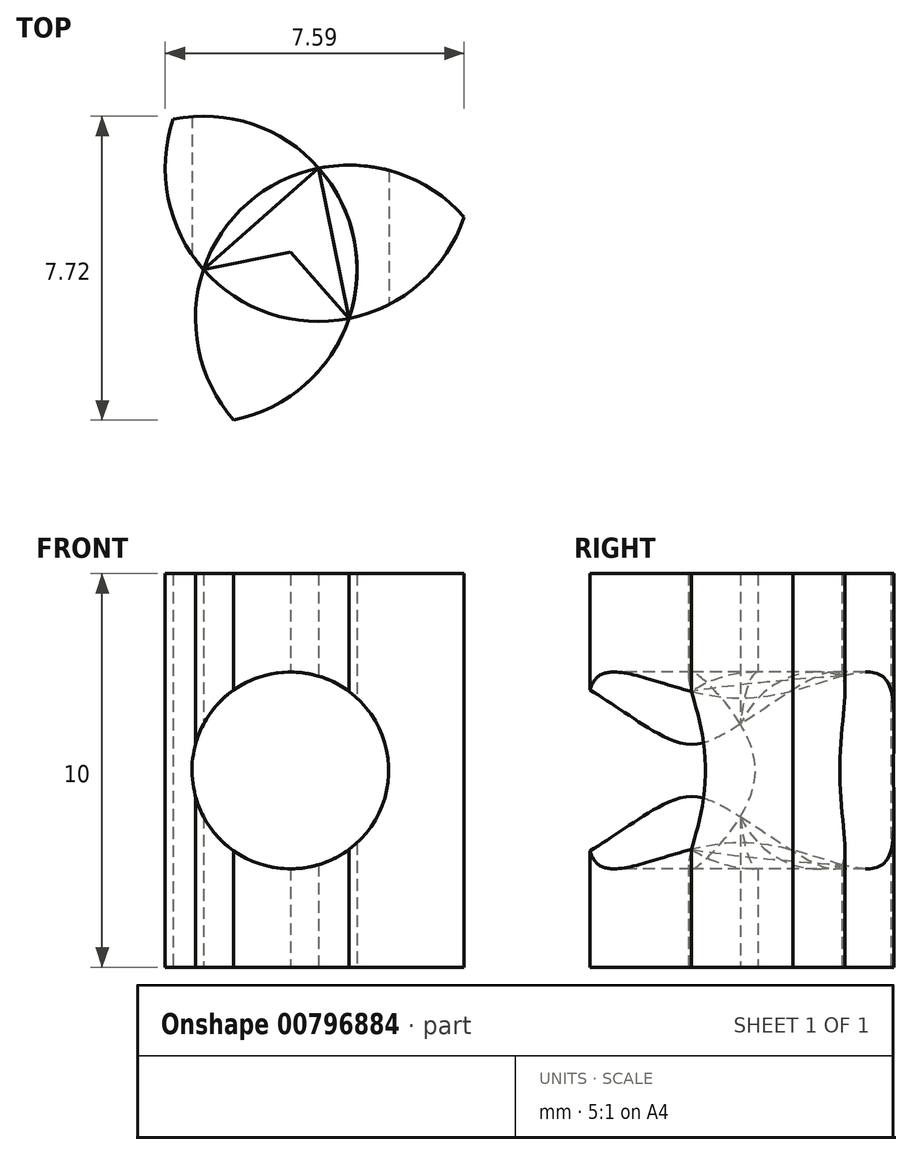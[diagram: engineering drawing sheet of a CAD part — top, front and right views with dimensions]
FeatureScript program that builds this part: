
annotation { "Feature Type Name" : "Feature", "Feature Type Description" : "" }
export const myFeature = defineFeature(function(context is Context, id is Id, definition is map)
    precondition{}
    {
        {
            var Q0;
            Q0=qCreatedBy(makeId("Top.planeOp"),FACE);
            var sketch = newSketch(context, id + "F0", { "sketchPlane" : qUnion([Q0])});
            skCircle(sketch, "E0", {"center": v(-2.2, -0.44) * mm, "radius": 3.9 * mm});
            skCircle(sketch, "E1", {"center": v(1.49, -1.69) * mm, "radius": 3.9 * mm});
            skCircle(sketch, "E2", {"center": v(0.72, 2.13) * mm, "radius": 3.9 * mm});
            skLineSegment(sketch, "E3", {"start": v(0.72, 2.13) * mm, "end": v(1.49, -1.69) * mm});
            skLineSegment(sketch, "E4", {"start": v(0.72, 2.13) * mm, "end": v(-2.2, -0.44) * mm});
            skLineSegment(sketch, "E5", {"start": v(1.1, 0.22) * mm, "end": v(-2.2, -0.44) * mm});
            skLineSegment(sketch, "E6", {"start": v(-0.74, 0.84) * mm, "end": v(1.49, -1.69) * mm});
            skLineSegment(sketch, "E7", {"start": v(0, 0) * mm, "end": v(0.72, 2.13) * mm});
            skPoint(sketch, "E8", {"position": v(0, 0) * mm});
            skPoint(sketch, "E9.end.orphan", {"position": v(-0.36, -1.07) * mm});
            skSolve(sketch);
        }
        {
            var Q0;
            {var subQ2=sQuery(id+"F0.wireOp",EDGE,"E0");var subQ4=sQuery(id+"F0.wireOp",EDGE,"E2");var subQ5=makeQuery(id+"F0.imprint","INTERSECT",VERTEX,{"derivedFrom":[subQ2,subQ4]});Q0=makeQuery(id+"F0.imprint","IMPRINT",FACE,{"disambiguationData":[TD([[makeQuery(id+"F0.imprint","IMPRINT",EDGE,{"disambiguationData":[TD([[subQ5,1.0]])],"derivedFrom":subQ2}),1.0]])]});}
            var Q1;
            {var subQ2=sQuery(id+"F0.wireOp",EDGE,"E0");var subQ4=sQuery(id+"F0.wireOp",EDGE,"E1");var subQ5=makeQuery(id+"F0.imprint","INTERSECT",VERTEX,{"derivedFrom":[subQ2,subQ4]});Q1=makeQuery(id+"F0.imprint","IMPRINT",FACE,{"disambiguationData":[TD([[makeQuery(id+"F0.imprint","IMPRINT",EDGE,{"disambiguationData":[TD([[subQ5,-1.0]])],"derivedFrom":subQ2}),1.0]])]});}
            var Q2;
            {var subQ1=sQuery(id+"F0.wireOp",EDGE,"E1");var subQ4=sQuery(id+"F0.wireOp",EDGE,"E2");var subQ6=makeQuery(id+"F0.imprint","INTERSECT",VERTEX,{"derivedFrom":[subQ1,subQ4]});Q2=makeQuery(id+"F0.imprint","IMPRINT",FACE,{"disambiguationData":[TD([[makeQuery(id+"F0.imprint","IMPRINT",EDGE,{"disambiguationData":[TD([[subQ6,-1.0]])],"derivedFrom":subQ1}),1.0]])]});}
            var Q3;
            {var subQ1=sQuery(id+"F0.wireOp",EDGE,"E9");var subQ3=sQuery(id+"F0.wireOp",EDGE,"E7");var subQ4=makeQuery(id+"F0.imprint","INTERSECT",VERTEX,{"derivedFrom":[subQ1,subQ3]});Q3=makeQuery(id+"F0.imprint","IMPRINT",FACE,{"disambiguationData":[TD([[makeQuery(id+"F0.imprint","IMPRINT",EDGE,{"disambiguationData":[TD([[subQ4,-1.0]])],"derivedFrom":subQ3}),-1.0]])]});}
            var Q4;
            {var subQ1=sQuery(id+"F0.wireOp",EDGE,"E3");var subQ3=sQuery(id+"F0.wireOp",EDGE,"E5");var subQ4=makeQuery(id+"F0.imprint","INTERSECT",VERTEX,{"derivedFrom":[subQ1,subQ3]});Q4=makeQuery(id+"F0.imprint","IMPRINT",FACE,{"disambiguationData":[TD([[makeQuery(id+"F0.imprint","IMPRINT",EDGE,{"disambiguationData":[TD([[subQ4,-1.0]])],"derivedFrom":subQ3}),1.0]])]});}
            var Q5;
            {var subQ1=sQuery(id+"F0.wireOp",EDGE,"E3");var subQ3=sQuery(id+"F0.wireOp",EDGE,"E5");var subQ4=makeQuery(id+"F0.imprint","INTERSECT",VERTEX,{"derivedFrom":[subQ1,subQ3]});Q5=makeQuery(id+"F0.imprint","IMPRINT",FACE,{"disambiguationData":[TD([[makeQuery(id+"F0.imprint","IMPRINT",EDGE,{"disambiguationData":[TD([[subQ4,-1.0]])],"derivedFrom":subQ3}),-1.0]])]});}
            var Q6;
            {var subQ1=sQuery(id+"F0.wireOp",EDGE,"E4");var subQ3=sQuery(id+"F0.wireOp",EDGE,"E6");var subQ4=makeQuery(id+"F0.imprint","INTERSECT",VERTEX,{"derivedFrom":[subQ1,subQ3]});Q6=makeQuery(id+"F0.imprint","IMPRINT",FACE,{"disambiguationData":[TD([[makeQuery(id+"F0.imprint","IMPRINT",EDGE,{"disambiguationData":[TD([[subQ4,-1.0]])],"derivedFrom":subQ3}),1.0]])]});}
            var Q7;
            {var subQ1=sQuery(id+"F0.wireOp",EDGE,"E4");var subQ3=sQuery(id+"F0.wireOp",EDGE,"E6");var subQ4=makeQuery(id+"F0.imprint","INTERSECT",VERTEX,{"derivedFrom":[subQ1,subQ3]});Q7=makeQuery(id+"F0.imprint","IMPRINT",FACE,{"disambiguationData":[TD([[makeQuery(id+"F0.imprint","IMPRINT",EDGE,{"disambiguationData":[TD([[subQ4,-1.0]])],"derivedFrom":subQ3}),-1.0]])]});}
            var Q8;
            {var subQ1=sQuery(id+"F0.wireOp",EDGE,"E9");var subQ3=sQuery(id+"F0.wireOp",EDGE,"E7");var subQ4=makeQuery(id+"F0.imprint","INTERSECT",VERTEX,{"derivedFrom":[subQ1,subQ3]});Q8=makeQuery(id+"F0.imprint","IMPRINT",FACE,{"disambiguationData":[TD([[makeQuery(id+"F0.imprint","IMPRINT",EDGE,{"disambiguationData":[TD([[subQ4,-1.0]])],"derivedFrom":subQ3}),1.0]])]});}
            extrude(context, id + "F1", {"entities" : qUnion([Q0, Q1, Q2, Q3, Q4, Q5, Q6, Q7, Q8]), "depth" : 10 * mm, "offsetDistance" : 25.4 * mm});
        }
        {
            var Q0;
            {var subQ0=sQuery(id+"F0.wireOp",EDGE,"E6");var subQ3=sQuery(id+"F0.wireOp",EDGE,"E5");var subQ5=makeQuery(id+"F0.imprint","INTERSECT",VERTEX,{"derivedFrom":[subQ3,subQ0,sQuery(id+"F0.wireOp",EDGE,"E7")]});Q0=makeQuery(id+"F0.imprint","IMPRINT",FACE,{"disambiguationData":[TD([[makeQuery(id+"F0.imprint","IMPRINT",EDGE,{"disambiguationData":[TD([[subQ5,-1.0]])],"derivedFrom":subQ3}),1.0]])]});}
            var Q1;
            {var subQ0=sQuery(id+"F0.wireOp",EDGE,"E4");var subQ1=sQuery(id+"F0.wireOp",EDGE,"E2");var subQ2=sQuery(id+"F0.wireOp",EDGE,"E1");var subQ3=makeQuery(id+"F0.imprint","INTERSECT",VERTEX,{"derivedFrom":[subQ2,subQ1,subQ0,sQuery(id+"F0.wireOp",EDGE,"E5")]});var subQ4=sQuery(id+"F0.wireOp",EDGE,"E0");var subQ5=makeQuery(id+"F0.imprint","INTERSECT",VERTEX,{"derivedFrom":[subQ4,subQ1]});Q1=makeQuery(id+"F1.opExtrude","CAP_FACE",FACE,{"disambiguationData":[OSD([subQ4,subQ2,subQ1]),TDD([makeQuery(id+"F0.imprint","IMPRINT",EDGE,{"disambiguationData":[TD([[subQ5,1.0]])],"derivedFrom":subQ4}),makeQuery(id+"F0.imprint","IMPRINT",EDGE,{"disambiguationData":[TD([[subQ3,1.0]])],"derivedFrom":subQ2}),makeQuery(id+"F0.imprint","IMPRINT",EDGE,{"disambiguationData":[TD([[subQ5,-1.0]])],"derivedFrom":subQ1})])],"isStart":false});}
            extrude(context, id + "F2", {"entities" : qUnion([Q0]), "endBound" : BoundingType.UP_TO_SURFACE, "depth" : 25 * mm, "endBoundEntityFace" : qUnion([Q1]), "offsetDistance" : 25 * mm});
        }
        {
            var Q0;
            Q0=qCreatedBy(makeId("Front.planeOp"),FACE);
            var sketch = newSketch(context, id + "F3", { "sketchPlane" : qUnion([Q0])});
            skCircle(sketch, "E10", {"center": v(0, 5) * mm, "radius": 2.5 * mm});
            skSolve(sketch);
        }
        {
            var Q0;
            Q0 = qSketchRegion(id + "F3", true);
            extrude(context, id + "F4", {"entities" : qUnion([Q0]), "operationType" : NewBodyOperationType.REMOVE, "endBound" : BoundingType.SYMMETRIC, "oppositeDirection" : true, "depth" : 25 * mm, "offsetDistance" : 25 * mm});
        }
    });
